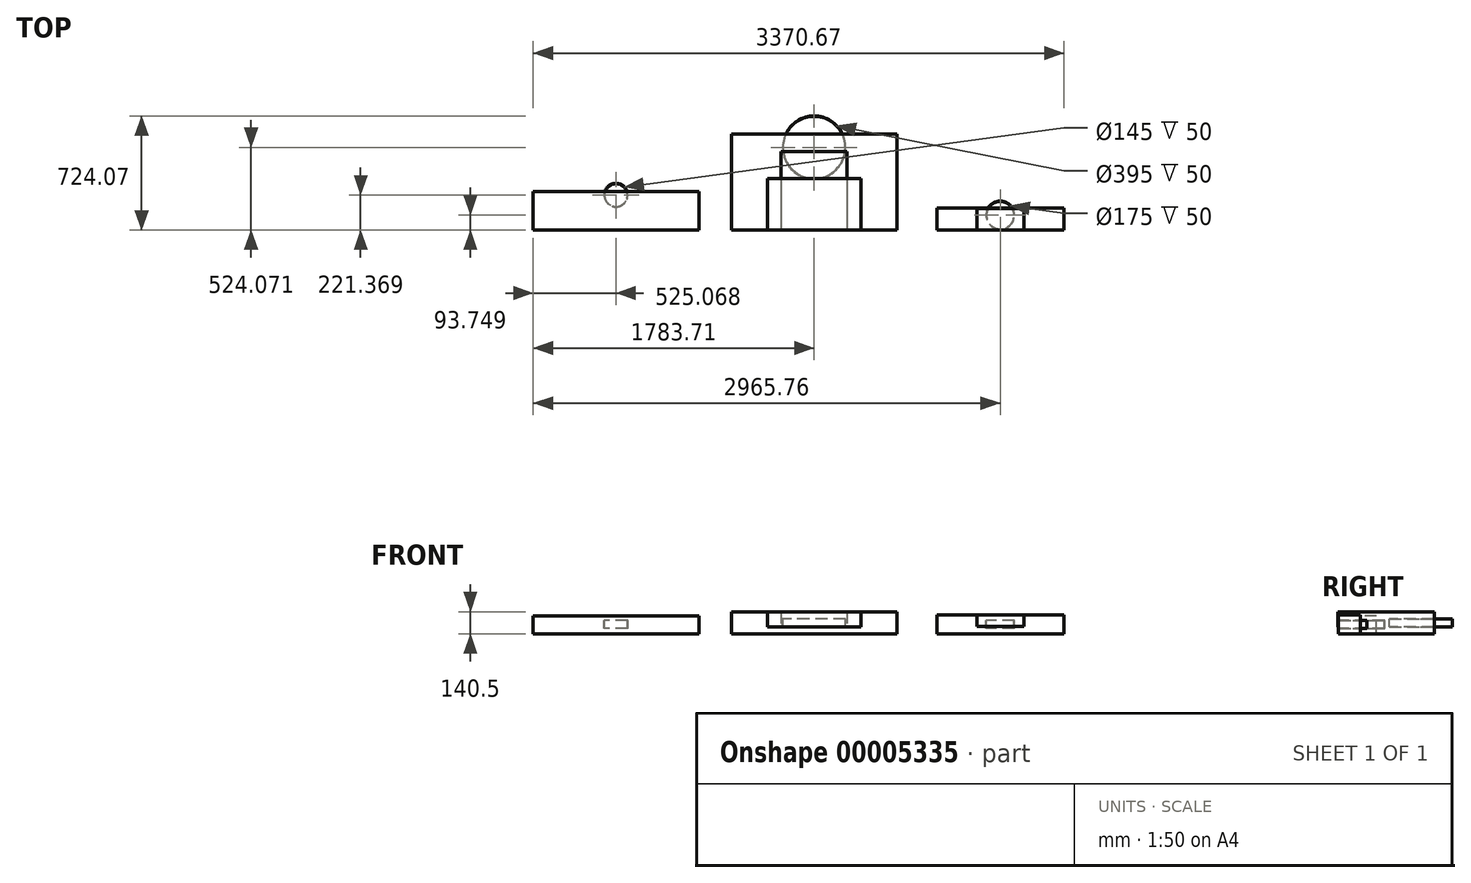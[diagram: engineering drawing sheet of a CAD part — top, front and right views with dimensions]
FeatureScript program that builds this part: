
annotation { "Feature Type Name" : "Feature", "Feature Type Description" : "" }
export const myFeature = defineFeature(function(context is Context, id is Id, definition is map)
    precondition{}
    {
        {
            var Q0;
            Q0=qCreatedBy(makeId("Front.planeOp"),FACE);
            var sketch = newSketch(context, id + "F0", { "sketchPlane" : qUnion([Q0])});
            skLineSegment(sketch, "E0.rect.bottom", {"start": v(525, -70) * mm, "end": v(-525, -70) * mm});
            skLineSegment(sketch, "E0.rect.top", {"start": v(525, 70) * mm, "end": v(-525, 70) * mm});
            skLineSegment(sketch, "E0.rect.left", {"start": v(525, -70) * mm, "end": v(525, 70) * mm});
            skLineSegment(sketch, "E0.rect.right", {"start": v(-525, -70) * mm, "end": v(-525, 70) * mm});
            skPoint(sketch, "E0.rect.middle", {"position": v(0, 0) * mm});
            skLineSegment(sketch, "E1.bottom", {"start": v(778.96, -70) * mm, "end": v(1586.96, -70) * mm});
            skLineSegment(sketch, "E1.top", {"start": v(778.96, 50) * mm, "end": v(1586.96, 50) * mm});
            skLineSegment(sketch, "E1.left", {"start": v(778.96, -70) * mm, "end": v(778.96, 50) * mm});
            skLineSegment(sketch, "E1.right", {"start": v(1586.96, -70) * mm, "end": v(1586.96, 50) * mm});
            skLineSegment(sketch, "E2.rect.bottom", {"start": v(-731.7, -70) * mm, "end": v(-1783.7, -70) * mm});
            skLineSegment(sketch, "E2.rect.top", {"start": v(-731.7, 43) * mm, "end": v(-1783.7, 43) * mm});
            skLineSegment(sketch, "E2.rect.right", {"start": v(-1783.7, -70) * mm, "end": v(-1783.7, 43) * mm});
            skPoint(sketch, "E2.rect.middle", {"position": v(-1257.7, -13.5) * mm});
            skLineSegment(sketch, "E2.rect.left", {"start": v(-731.7, -70) * mm, "end": v(-731.7, 43) * mm});
            skLineSegment(sketch, "E3", {"start": v(-525, -70) * mm, "end": v(-731.7, -70) * mm, "construction": true});
            skSolve(sketch);
        }
        {
            var Q0;
            Q0=makeQuery(id+"F0.imprint","IMPRINT",FACE,{"disambiguationData":[TD([[makeQuery(id+"F0.imprint","IMPRINT",EDGE,{"derivedFrom":sQuery(id+"F0.wireOp",EDGE,"E0.rect.bottom")}),-1.0]])]});
            extrude(context, id + "F1", {"entities" : qUnion([Q0]), "oppositeDirection" : true, "depth" : 610 * mm});
        }
        {
            var Q0;
            Q0=makeQuery(id+"F1.opExtrude","SWEPT_FACE",FACE,{"disambiguationData":[OSD([sQuery(id+"F0.wireOp",EDGE,"E0.rect.top")])]});
            var sketch = newSketch(context, id + "F2", { "sketchPlane" : qUnion([Q0])});
            skLineSegment(sketch, "E4.bottom", {"start": v(-297, 325) * mm, "end": v(297, 325) * mm});
            skLineSegment(sketch, "E4.top", {"start": v(-297, 0) * mm, "end": v(297, 0) * mm});
            skLineSegment(sketch, "E4.left", {"start": v(-297, 325) * mm, "end": v(-297, 0) * mm});
            skLineSegment(sketch, "E4.right", {"start": v(297, 325) * mm, "end": v(297, 0) * mm});
            skPoint(sketch, "E5", {"position": v(0, 0) * mm});
            skLineSegment(sketch, "E6", {"start": v(0, 0) * mm, "end": v(0, -61.2) * mm, "construction": true});
            skSolve(sketch);
        }
        {
            var Q0;
            Q0=makeQuery(id+"F1.opExtrude","CAP_FACE",FACE,{"disambiguationData":[OSD([sQuery(id+"F0.wireOp",EDGE,"E0.rect.bottom"),sQuery(id+"F0.wireOp",EDGE,"E0.rect.top"),sQuery(id+"F0.wireOp",EDGE,"E0.rect.left"),sQuery(id+"F0.wireOp",EDGE,"E0.rect.right")])],"isStart":true});
            var sketch = newSketch(context, id + "F3", { "sketchPlane" : qUnion([Q0])});
            skLineSegment(sketch, "E7.bottom", {"start": v(-297, 70) * mm, "end": v(297, 70) * mm});
            skLineSegment(sketch, "E7.top", {"start": v(-297, -25) * mm, "end": v(297, -25) * mm});
            skLineSegment(sketch, "E7.left", {"start": v(-297, 70) * mm, "end": v(-297, -25) * mm});
            skLineSegment(sketch, "E7.right", {"start": v(297, 70) * mm, "end": v(297, -25) * mm});
            skSolve(sketch);
        }
        {
            var Q0;
            Q0=makeQuery(id+"F0.imprint","IMPRINT",FACE,{"disambiguationData":[TD([[makeQuery(id+"F0.imprint","IMPRINT",EDGE,{"derivedFrom":sQuery(id+"F0.wireOp",EDGE,"E1.bottom")}),1.0]])]});
            extrude(context, id + "F4", {"entities" : qUnion([Q0]), "oppositeDirection" : true, "depth" : 140 * mm});
        }
        {
            var Q0;
            Q0=makeQuery(id+"F4.opExtrude","SWEPT_FACE",FACE,{"disambiguationData":[OSD([sQuery(id+"F0.wireOp",EDGE,"E1.top")])]});
            var sketch = newSketch(context, id + "F5", { "sketchPlane" : qUnion([Q0])});
            skLineSegment(sketch, "E8.bottom", {"start": v(1034.46, 136) * mm, "end": v(1331.46, 136) * mm});
            skLineSegment(sketch, "E8.top", {"start": v(1034.46, 0) * mm, "end": v(1331.46, 0) * mm});
            skLineSegment(sketch, "E8.left", {"start": v(1034.46, 136) * mm, "end": v(1034.46, 0) * mm});
            skLineSegment(sketch, "E8.right", {"start": v(1331.46, 136) * mm, "end": v(1331.46, 0) * mm});
            skPoint(sketch, "E9", {"position": v(1182.96, 0) * mm});
            skSolve(sketch);
        }
        {
            var Q0;
            Q0 = qSketchRegion(id + "F2", true);
            var Q1;
            Q1=makeQuery(id+"F5.imprint","IMPRINT",FACE,{"disambiguationData":[TD([[makeQuery(id+"F5.imprint","IMPRINT",EDGE,{"derivedFrom":sQuery(id+"F5.wireOp",EDGE,"E8.bottom")}),-1.0]])]});
            extrude(context, id + "F6", {"entities" : qUnion([Q0, Q1]), "depth" : 0.5 * mm});
        }
        {
            var Q0;
            Q0=makeQuery(id+"F4.opExtrude","CAP_FACE",FACE,{"disambiguationData":[OSD([sQuery(id+"F0.wireOp",EDGE,"E1.bottom"),sQuery(id+"F0.wireOp",EDGE,"E1.top"),sQuery(id+"F0.wireOp",EDGE,"E1.left"),sQuery(id+"F0.wireOp",EDGE,"E1.right")])],"isStart":true});
            var sketch = newSketch(context, id + "F7", { "sketchPlane" : qUnion([Q0])});
            skLineSegment(sketch, "E10.bottom", {"start": v(1034.46, 50.5) * mm, "end": v(1331.46, 50.5) * mm});
            skLineSegment(sketch, "E10.top", {"start": v(1034.46, -23.5) * mm, "end": v(1331.46, -23.5) * mm});
            skLineSegment(sketch, "E10.left", {"start": v(1034.46, 50.5) * mm, "end": v(1034.46, -23.5) * mm});
            skLineSegment(sketch, "E10.right", {"start": v(1331.46, 50.5) * mm, "end": v(1331.46, -23.5) * mm});
            skSolve(sketch);
        }
        {
            var Q0;
            Q0=makeQuery(id+"F3.imprint","IMPRINT",FACE,{"disambiguationData":[TD([[makeQuery(id+"F3.imprint","IMPRINT",EDGE,{"derivedFrom":sQuery(id+"F3.wireOp",EDGE,"E7.bottom")}),1.0]])]});
            var Q1;
            {var subQ5=sQuery(id+"F7.wireOp",EDGE,"E10.top");Q1=makeQuery(id+"F7.imprint","IMPRINT",FACE,{"disambiguationData":[TD([[makeQuery(id+"F7.imprint","IMPRINT",EDGE,{"derivedFrom":subQ5}),1.0]])]});}
            extrude(context, id + "F8", {"entities" : qUnion([Q0, Q1]), "depth" : 0.5 * mm});
        }
        {
            var Q0;
            Q0=makeQuery(id+"F1.opExtrude","SWEPT_FACE",FACE,{"disambiguationData":[OSD([sQuery(id+"F0.wireOp",EDGE,"E0.rect.top")])]});
            var sketch = newSketch(context, id + "F9", { "sketchPlane" : qUnion([Q0])});
            skLineSegment(sketch, "E11.bottom", {"start": v(-209.5, 497) * mm, "end": v(209.5, 497) * mm});
            skLineSegment(sketch, "E11.top", {"start": v(-209.5, 0) * mm, "end": v(209.5, 0) * mm});
            skLineSegment(sketch, "E11.left", {"start": v(-209.5, 497) * mm, "end": v(-209.5, 0) * mm});
            skLineSegment(sketch, "E11.right", {"start": v(209.5, 497) * mm, "end": v(209.5, 0) * mm});
            skPoint(sketch, "E12", {"position": v(0, 0) * mm});
            skLineSegment(sketch, "E13", {"start": v(0, 0) * mm, "end": v(0, -123.88) * mm, "construction": true});
            skSolve(sketch);
        }
        {
            var Q0;
            Q0=makeQuery(id+"F9.imprint","IMPRINT",FACE,{"disambiguationData":[TD([[makeQuery(id+"F9.imprint","IMPRINT",EDGE,{"derivedFrom":sQuery(id+"F9.wireOp",EDGE,"E11.bottom")}),-1.0]])]});
            extrude(context, id + "F10", {"entities" : qUnion([Q0]), "depth" : 0.2 * mm});
        }
        {
            var Q0;
            Q0=makeQuery(id+"F1.opExtrude","CAP_FACE",FACE,{"disambiguationData":[OSD([sQuery(id+"F0.wireOp",EDGE,"E0.rect.bottom"),sQuery(id+"F0.wireOp",EDGE,"E0.rect.top"),sQuery(id+"F0.wireOp",EDGE,"E0.rect.left"),sQuery(id+"F0.wireOp",EDGE,"E0.rect.right")])],"isStart":true});
            var sketch = newSketch(context, id + "F11", { "sketchPlane" : qUnion([Q0])});
            skLineSegment(sketch, "E14.bottom", {"start": v(-209.5, 70) * mm, "end": v(209.5, 70) * mm});
            skLineSegment(sketch, "E14.top", {"start": v(-209.5, -25) * mm, "end": v(209.5, -25) * mm});
            skLineSegment(sketch, "E14.left", {"start": v(-209.5, 70) * mm, "end": v(-209.5, -25) * mm});
            skLineSegment(sketch, "E14.right", {"start": v(209.5, 70) * mm, "end": v(209.5, -25) * mm});
            skSolve(sketch);
        }
        {
            var Q0;
            Q0=makeQuery(id+"F11.imprint","IMPRINT",FACE,{"disambiguationData":[TD([[makeQuery(id+"F11.imprint","IMPRINT",EDGE,{"derivedFrom":sQuery(id+"F11.wireOp",EDGE,"E14.bottom")}),1.0]])]});
            extrude(context, id + "F12", {"entities" : qUnion([Q0]), "depth" : 0.2 * mm});
        }
        {
            var Q0;
            Q0=makeQuery(id+"F0.imprint","IMPRINT",FACE,{"disambiguationData":[TD([[makeQuery(id+"F0.imprint","IMPRINT",EDGE,{"derivedFrom":sQuery(id+"F0.wireOp",EDGE,"E2.rect.bottom")}),-1.0]])]});
            extrude(context, id + "F13", {"entities" : qUnion([Q0]), "oppositeDirection" : true, "depth" : 244 * mm});
        }
        {
            var Q0;
            Q0=makeQuery(id+"F1.opExtrude","SWEPT_FACE",FACE,{"disambiguationData":[OSD([sQuery(id+"F0.wireOp",EDGE,"E0.rect.top")])]});
            var sketch = newSketch(context, id + "F14", { "sketchPlane" : qUnion([Q0])});
            skCircle(sketch, "E15", {"center": v(0, 523.57) * mm, "radius": 200 * mm});
            skCircle(sketch, "E16", {"center": v(1182.05, 93.25) * mm, "radius": 90 * mm});
            skCircle(sketch, "E17", {"center": v(-1258.64, 220.87) * mm, "radius": 75 * mm});
            skSolve(sketch);
        }
        {
            var Q0;
            Q0 = qSketchRegion(id + "F14", true);
            extrude(context, id + "F15", {"entities" : qUnion([Q0]), "oppositeDirection" : true, "depth" : 50 * mm});
        }
        {
            var Q0;
            Q0=makeQuery(id+"F15.opExtrude","CAP_FACE",FACE,{"disambiguationData":[OSD([sQuery(id+"F14.wireOp",EDGE,"E15")])],"isStart":true});
            var Q1;
            Q1=makeQuery(id+"F15.opExtrude","CAP_FACE",FACE,{"disambiguationData":[OSD([sQuery(id+"F14.wireOp",EDGE,"E15")])],"isStart":false});
            var Q2;
            Q2=makeQuery(id+"F15.opExtrude","CAP_FACE",FACE,{"disambiguationData":[OSD([sQuery(id+"F14.wireOp",EDGE,"E16")])],"isStart":true});
            var Q3;
            Q3=makeQuery(id+"F15.opExtrude","CAP_FACE",FACE,{"disambiguationData":[OSD([sQuery(id+"F14.wireOp",EDGE,"E16")])],"isStart":false});
            var Q4;
            Q4=makeQuery(id+"F15.opExtrude","CAP_FACE",FACE,{"disambiguationData":[OSD([sQuery(id+"F14.wireOp",EDGE,"E17")])],"isStart":true});
            var Q5;
            Q5=makeQuery(id+"F15.opExtrude","CAP_FACE",FACE,{"disambiguationData":[OSD([sQuery(id+"F14.wireOp",EDGE,"E17")])],"isStart":false});
            shell(context, id + "F16", {"entities" : qUnion([Q0, Q1, Q2, Q3, Q4, Q5]), "thickness" : 2.5 * mm});
        }
        {
            var Q0;
            Q0=makeQuery(id+"F15.opExtrude","SWEPT_BODY",BODY,{"disambiguationData":[OSD([sQuery(id+"F14.wireOp",EDGE,"E16")])]});
            transform(context, id + "F17", {"entities" : qUnion([Q0]), "transformType" : TransformType.TRANSLATION_3D, "dx" : 0 * mm, "dy" : 0 * mm, "dz" : -54.53 * mm, "makeCopy" : false});
        }
        {
            var Q0;
            Q0=makeQuery(id+"F15.opExtrude","SWEPT_BODY",BODY,{"disambiguationData":[OSD([sQuery(id+"F14.wireOp",EDGE,"E15")])]});
            transform(context, id + "F18", {"entities" : qUnion([Q0]), "transformType" : TransformType.TRANSLATION_3D, "dx" : 0 * mm, "dy" : 0 * mm, "dz" : -45 * mm, "makeCopy" : false});
        }
        {
            var Q0;
            Q0=makeQuery(id+"F15.opExtrude","SWEPT_BODY",BODY,{"disambiguationData":[OSD([sQuery(id+"F14.wireOp",EDGE,"E17")])]});
            transform(context, id + "F19", {"entities" : qUnion([Q0]), "transformType" : TransformType.TRANSLATION_3D, "dx" : 0 * mm, "dy" : 0 * mm, "dz" : -54.4 * mm, "makeCopy" : false});
        }
    });
